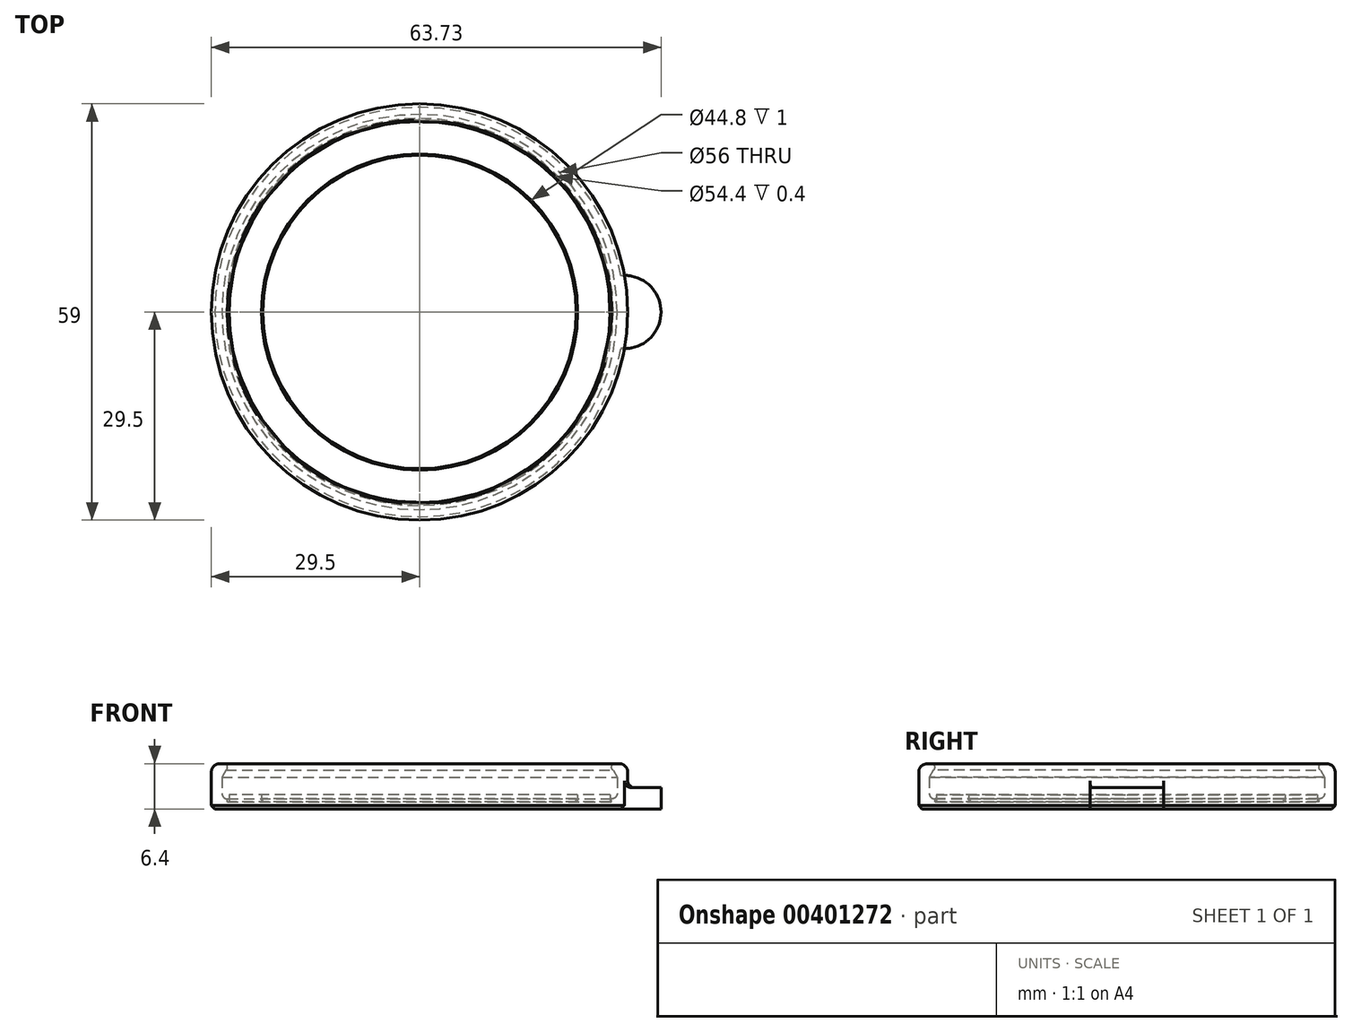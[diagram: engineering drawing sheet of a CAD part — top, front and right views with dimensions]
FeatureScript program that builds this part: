
annotation { "Feature Type Name" : "Feature", "Feature Type Description" : "" }
export const myFeature = defineFeature(function(context is Context, id is Id, definition is map)
    precondition{}
    {
        {
            var Q0;
            Q0=qCreatedBy(makeId("Front.planeOp"),FACE);
            var sketch = newSketch(context, id + "F0", { "sketchPlane" : qUnion([Q0])});
            skLineSegment(sketch, "E0", {"start": v(0, 0) * mm, "end": v(0, 1.4) * mm});
            skLineSegment(sketch, "E1", {"start": v(0, 1.4) * mm, "end": v(27.2, 1.4) * mm});
            skLineSegment(sketch, "E2", {"start": v(27.2, 6.4) * mm, "end": v(28.3, 6.4) * mm});
            skLineSegment(sketch, "E3", {"start": v(29.5, 5.2) * mm, "end": v(29.5, 0) * mm});
            skLineSegment(sketch, "E4", {"start": v(29.5, 0) * mm, "end": v(0, 0) * mm});
            skLineSegment(sketch, "E5", {"start": v(27.2, 6.4) * mm, "end": v(27.2, 5.4) * mm});
            skLineSegment(sketch, "E6", {"start": v(28, 5.4) * mm, "end": v(28, 2.2) * mm});
            skLineSegment(sketch, "E7", {"start": v(27.2, 1.4) * mm, "end": v(27.2, 1.4) * mm});
            skPoint(sketch, "E8.visualSharp", {"position": v(28, 5.3) * mm});
            skPoint(sketch, "E9.visualSharp", {"position": v(28, 1.4) * mm});
            skArc(sketch, "E9.filletArc", {"start": v(27.2, 1.4) * mm, "mid": v(27.77, 1.63) * mm, "end": v(28, 2.2) * mm});
            skPoint(sketch, "E10.visualSharp", {"position": v(29.5, 6.4) * mm});
            skArc(sketch, "E10.filletArc", {"start": v(29.5, 5.2) * mm, "mid": v(29.15, 6.05) * mm, "end": v(28.3, 6.4) * mm});
            skPoint(sketch, "E11.visualSharp", {"position": v(29.5, 0) * mm});
            skLineSegment(sketch, "E12", {"start": v(27.2, 5.4) * mm, "end": v(28, 5.4) * mm});
            skSolve(sketch);
        }
        {
            var Q0;
            Q0=qSketchRegion(id+"F0",true);
            var Q1;
            Q1=sQuery(id+"F0.wireOp",EDGE,"E0");
            revolve(context, id + "F1", {"entities" : qUnion([Q0]), "axis" : qUnion([Q1]), "revolveType" : RevolveType.FULL});
        }
        {
            var Q0;
            Q0=makeQuery(id+"F1.opRevolve","SWEPT_EDGE",EDGE,{"disambiguationData":[OSD([sQuery(id+"F0.wireOp",EDGE,"E2"),sQuery(id+"F0.wireOp",EDGE,"E5")])]});
            var Q1;
            Q1=makeQuery(id+"F1.opRevolve","SWEPT_EDGE",EDGE,{"disambiguationData":[OSD([sQuery(id+"F0.wireOp",EDGE,"E5"),sQuery(id+"F0.wireOp",EDGE,"caB6Z0El-ZOFv-nd8C-T2XF-bNLPoTO0AisI")])]});
            fillet(context, id + "F2", {"entities" : qUnion([Q0, Q1]), "radius" : .5 * mm, "tangentPropagation" : true, "allowEdgeOverflow" : false});
        }
        {
            var Q0;
            Q0=qCreatedBy(makeId("Top.planeOp"),FACE);
            var sketch = newSketch(context, id + "F3", { "sketchPlane" : qUnion([Q0])});
            skLineSegment(sketch, "E13", {"start": v(29.04, 5.19) * mm, "end": v(29.04, -5.19) * mm});
            skPoint(sketch, "E14", {"position": v(29.04, 0) * mm});
            skArc(sketch, "E15", {"start": v(29.04, -5.19) * mm, "mid": v(34.23, 0) * mm, "end": v(29.04, 5.19) * mm});
            skSolve(sketch);
        }
        {
            var Q0;
            Q0=qSketchRegion(id+"F3",true);
            extrude(context, id + "F4", {"entities" : qUnion([Q0]), "operationType" : NewBodyOperationType.ADD, "depth" : 3 * mm});
        }
        {
            var Q0;
            Q0=makeQuery(id+"F4.boolean.opBoolean","INTERSECT",EDGE,{"derivedFrom":[makeQuery(id+"F1.opRevolve","SWEPT_FACE",FACE,{"disambiguationData":[OSD([sQuery(id+"F0.wireOp",EDGE,"E3")])]}),makeQuery(id+"F4.opExtrude","CAP_FACE",FACE,{"disambiguationData":[OSD([sQuery(id+"F3.wireOp",EDGE,"E13"),sQuery(id+"F3.wireOp",EDGE,"E15")])],"isStart":false})]});
            var Q1;
            {var subQ0=sQuery(id+"F3.wireOp",EDGE,"E15");var subQ1=sQuery(id+"F3.wireOp",EDGE,"E13");Q1=makeQuery(id+"F4.opExtrude","SWEPT_EDGE",EDGE,{"disambiguationData":[OSD([subQ1,subQ0]),TDD([makeQuery(id+"F3.imprint","INTERSECT",VERTEX,{"disambiguationData":[OD(0.0)],"derivedFrom":[subQ1,subQ0]})])]});}
            var Q2;
            {var subQ0=sQuery(id+"F3.wireOp",EDGE,"E15");var subQ1=sQuery(id+"F3.wireOp",EDGE,"E13");Q2=makeQuery(id+"F4.opExtrude","SWEPT_EDGE",EDGE,{"disambiguationData":[OSD([subQ1,subQ0]),TDD([makeQuery(id+"F3.imprint","INTERSECT",VERTEX,{"disambiguationData":[OD(1.0)],"derivedFrom":[subQ1,subQ0]})])]});}
            fillet(context, id + "F5", {"entities" : qUnion([Q0, Q1, Q2]), "radius" : 1 * mm, "tangentPropagation" : true, "allowEdgeOverflow" : false});
        }
        {
            var Q0;
            Q0=makeQuery(id+"F1.opRevolve","SWEPT_EDGE",EDGE,{"disambiguationData":[OSD([sQuery(id+"F0.wireOp",EDGE,"E6"),sQuery(id+"F0.wireOp",EDGE,"E12")])]});
            chamfer(context, id + "F6", {"entities" : qUnion([Q0]), "width" : 1.2 * mm, "tangentPropagation" : true});
        }
        {
            var Q0;
            Q0=makeQuery(id+"F1.opRevolve","SWEPT_EDGE",EDGE,{"disambiguationData":[OSD([sQuery(id+"F0.wireOp",EDGE,"E3"),sQuery(id+"F0.wireOp",EDGE,"E4")])]});
            chamfer(context, id + "F7", {"entities" : qUnion([Q0]), "width" : .5 * mm, "tangentPropagation" : true});
        }
        {
            var Q0;
            Q0=makeQuery(id+"F1.opRevolve","SWEPT_FACE",FACE,{"disambiguationData":[OSD([sQuery(id+"F0.wireOp",EDGE,"E1"),sQuery(id+"F0.wireOp",EDGE,"E7")])]});
            var sketch = newSketch(context, id + "F8", { "sketchPlane" : qUnion([Q0])});
            skCircle(sketch, "E16", {"center": v(0, 0) * mm, "radius": 27.2 * mm});
            skCircle(sketch, "E17", {"center": v(0, 0) * mm, "radius": 22.2 * mm});
            skSolve(sketch);
        }
        {
            var Q0;
            Q0 = qSketchRegion(id + "F8", true);
            extrude(context, id + "F9", {"entities" : qUnion([Q0]), "operationType" : NewBodyOperationType.REMOVE, "oppositeDirection" : true, "depth" : .4 * mm});
        }
        {
            var Q0;
            Q0=makeQuery(id+"F9.boolean.opBoolean","COPY",FACE,{"derivedFrom":makeQuery(id+"F9.opExtrude","CAP_FACE",FACE,{"disambiguationData":[OSD([sQuery(id+"F8.wireOp",EDGE,"E16"),sQuery(id+"F8.wireOp",EDGE,"E17")])],"isStart":false})});
            var sketch = newSketch(context, id + "F10", { "sketchPlane" : qUnion([Q0])});
            skCircle(sketch, "E18.0", {"center": v(0, 0) * mm, "radius": 27 * mm});
            skCircle(sketch, "E19.0", {"center": v(0, 0) * mm, "radius": 22.4 * mm});
            skSolve(sketch);
        }
        {
            var Q0;
            Q0 = qSketchRegion(id + "F10", true);
            extrude(context, id + "F11", {"entities" : qUnion([Q0]), "depth" : 1 * mm});
        }
    });
